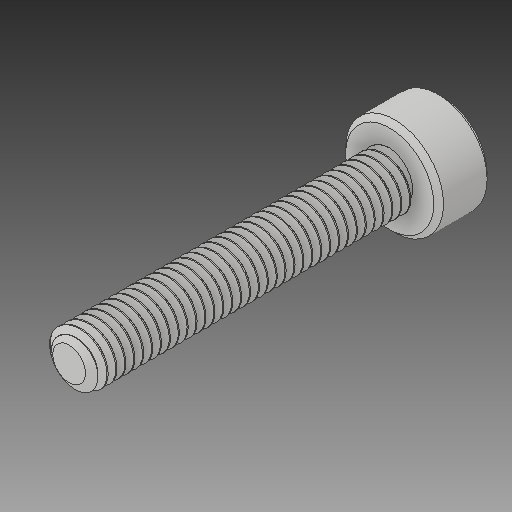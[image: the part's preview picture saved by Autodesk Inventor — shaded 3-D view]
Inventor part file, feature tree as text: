
AUTODESK INVENTOR PART (.ipt)
format: ipt  version: 2019.4 (Build 234330000, 330)  size: 1,146,368 bytes
history: native  units: in
note: dims shown in document units (in); Inventor stores cm internally (conversion verified against a paired STEP export)
features: chamfer x1
ambient origin geometry x8: Origin, YZ Plane, XZ Plane, XY Plane, X Axis, Y Axis, Z Axis, Center Point
bodies: Solid1 (feature_tree)
feature tree (1):
  chamfer  "Chamfer1"  [1 undecoded]
note: 1 required parameter value undecoded (feature->parameter linkage not recoverable at this tier; creation-order binding heuristic only, values carry confidence <= 0.55)
